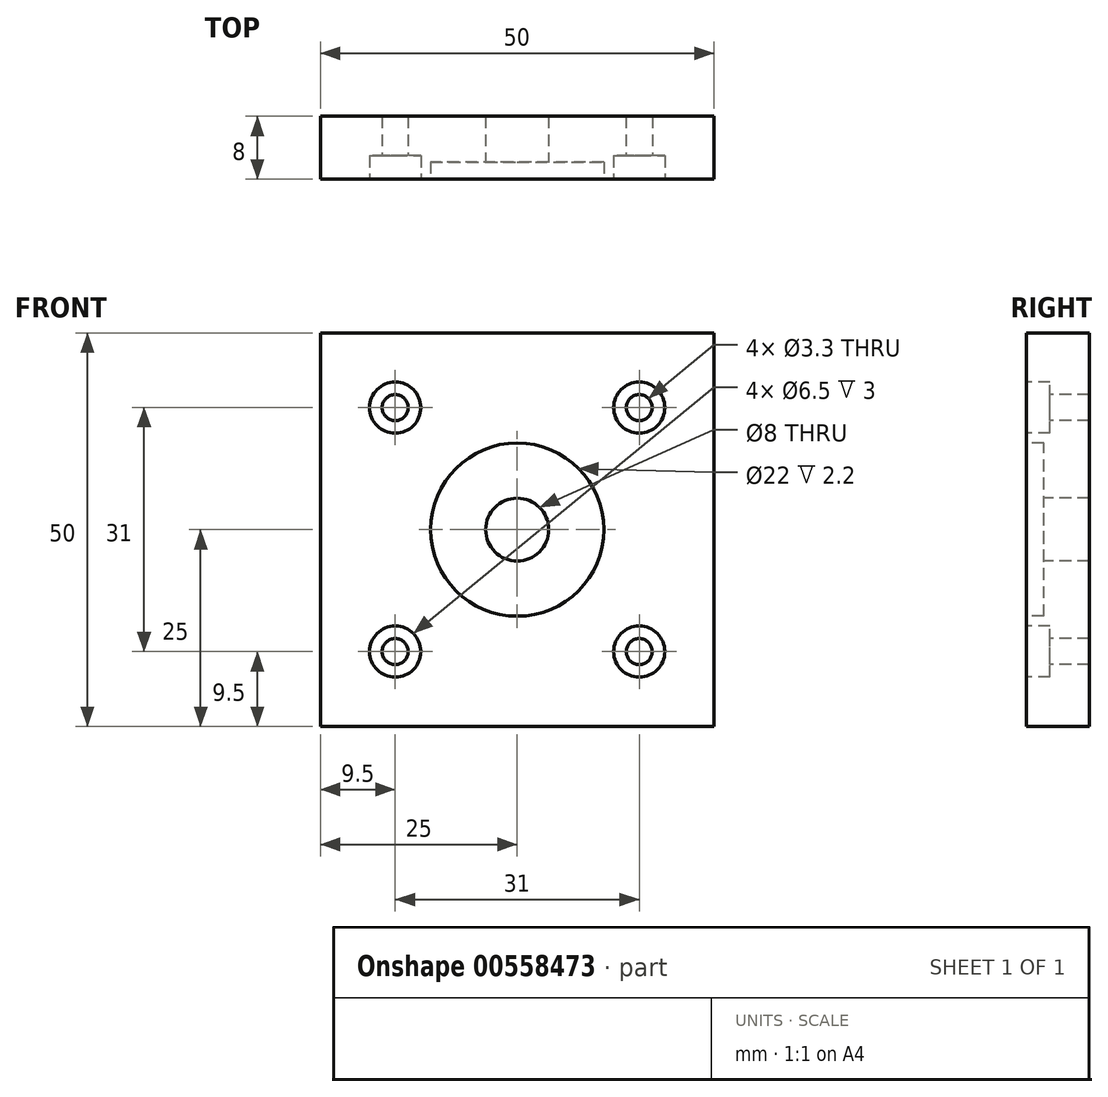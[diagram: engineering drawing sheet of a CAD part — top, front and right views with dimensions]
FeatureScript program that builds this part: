
annotation { "Feature Type Name" : "Feature", "Feature Type Description" : "" }
export const myFeature = defineFeature(function(context is Context, id is Id, definition is map)
    precondition{}
    {
        {
            var Q0;
            Q0=qCreatedBy(makeId("Front.planeOp"),FACE);
            var sketch = newSketch(context, id + "F0", { "sketchPlane" : qUnion([Q0])});
            skLineSegment(sketch, "E0.bottom", {"start": v(25, 25) * mm, "end": v(-25, 25) * mm});
            skLineSegment(sketch, "E0.top", {"start": v(25, -25) * mm, "end": v(-25, -25) * mm});
            skLineSegment(sketch, "E0.left", {"start": v(25, 25) * mm, "end": v(25, -25) * mm});
            skLineSegment(sketch, "E0.right", {"start": v(-25, 25) * mm, "end": v(-25, -25) * mm});
            skSolve(sketch);
        }
        {
            var Q0;
            Q0 = qSketchRegion(id + "F0", true);
            extrude(context, id + "F1", {"entities" : qUnion([Q0]), "depth" : 8 * mm, "offsetDistance" : 25 * mm});
        }
        {
            var Q0;
            Q0=makeQuery(id+"F1.opExtrude","CAP_FACE",FACE,{"disambiguationData":[OSD([sQuery(id+"F0.wireOp",EDGE,"E0.bottom"),sQuery(id+"F0.wireOp",EDGE,"E0.top"),sQuery(id+"F0.wireOp",EDGE,"E0.left"),sQuery(id+"F0.wireOp",EDGE,"E0.right")])],"isStart":false});
            var sketch = newSketch(context, id + "F2", { "sketchPlane" : qUnion([Q0])});
            skCircle(sketch, "E1", {"center": v(0, 0) * mm, "radius": 4 * mm});
            skSolve(sketch);
        }
        {
            var Q0;
            Q0=sQuery(id+"F2.wireOp",VERTEX,"E1.center");
            var Q1;
            Q1=makeQuery(id+"F1.opExtrude","SWEPT_BODY",BODY,{"disambiguationData":[OSD([sQuery(id+"F0.wireOp",EDGE,"E0.bottom"),sQuery(id+"F0.wireOp",EDGE,"E0.top"),sQuery(id+"F0.wireOp",EDGE,"E0.left"),sQuery(id+"F0.wireOp",EDGE,"E0.right")])]});
            hole(context, id + "F3", {"style" : HoleStyle.C_BORE, "endStyle" : HoleEndStyle.THROUGH, "holeDiameter" : 8 * mm, "cBoreDiameter" : 22 * mm, "cBoreDepth" : 2.2 * mm, "isTappedThrough" : true, "tappedDepth" : 12 * mm, "tapClearance" : 3, "locations" : qUnion([Q0]), "scope" : qUnion([Q1])});
        }
        {
            var Q0;
            Q0=makeQuery(id+"F1.opExtrude","CAP_FACE",FACE,{"disambiguationData":[OSD([sQuery(id+"F0.wireOp",EDGE,"E0.bottom"),sQuery(id+"F0.wireOp",EDGE,"E0.top"),sQuery(id+"F0.wireOp",EDGE,"E0.left"),sQuery(id+"F0.wireOp",EDGE,"E0.right")])],"isStart":false});
            var sketch = newSketch(context, id + "F4", { "sketchPlane" : qUnion([Q0])});
            skCircle(sketch, "E2", {"center": v(15.5, 15.5) * mm, "radius": 2 * mm});
            skLineSegment(sketch, "E3", {"start": v(0, 36.73) * mm, "end": v(0, -39.11) * mm, "construction": true});
            skPoint(sketch, "E3.endSnap0", {"position": v(0, -25) * mm});
            skCircle(sketch, "E4.MirrorC", {"center": v(-15.5, 15.5) * mm, "radius": 2 * mm});
            skLineSegment(sketch, "E5", {"start": v(-36.21, 0) * mm, "end": v(34.65, 0) * mm, "construction": true});
            skCircle(sketch, "E6.MirrorC", {"center": v(-15.5, -15.5) * mm, "radius": 2 * mm});
            skCircle(sketch, "E7.MirrorC", {"center": v(15.5, -15.5) * mm, "radius": 2 * mm});
            skSolve(sketch);
        }
        {
            var Q0;
            Q0=sQuery(id+"F4.wireOp",VERTEX,"E2.center");
            var Q1;
            Q1=sQuery(id+"F4.wireOp",VERTEX,"E4.MirrorC.center");
            var Q2;
            Q2=sQuery(id+"F4.wireOp",VERTEX,"E6.MirrorC.center");
            var Q3;
            Q3=sQuery(id+"F4.wireOp",VERTEX,"E7.MirrorC.center");
            var Q4;
            Q4=makeQuery(id+"F1.opExtrude","SWEPT_BODY",BODY,{"disambiguationData":[OSD([sQuery(id+"F0.wireOp",EDGE,"E0.bottom"),sQuery(id+"F0.wireOp",EDGE,"E0.top"),sQuery(id+"F0.wireOp",EDGE,"E0.left"),sQuery(id+"F0.wireOp",EDGE,"E0.right")])]});
            hole(context, id + "F5", {"style" : HoleStyle.C_BORE, "endStyle" : HoleEndStyle.THROUGH, "standardTappedOrClearance" : lookupTablePath({ "standard" : "ISO", "fit" : "Normal", "size" : "M3", "type" : "Clearance" }), "standardBlindInLast" : lookupTablePath({ "fit" : "Standard", "standard" : "ISO", "size" : "M3", "type" : "Clearance" }), "holeDiameter" : 3.3 * mm, "cBoreDiameter" : 6.5 * mm, "cBoreDepth" : 3 * mm, "isTappedThrough" : true, "tappedDepth" : 12 * mm, "tapClearance" : 3, "locations" : qUnion([Q0, Q1, Q2, Q3]), "scope" : qUnion([Q4])});
        }
    });
